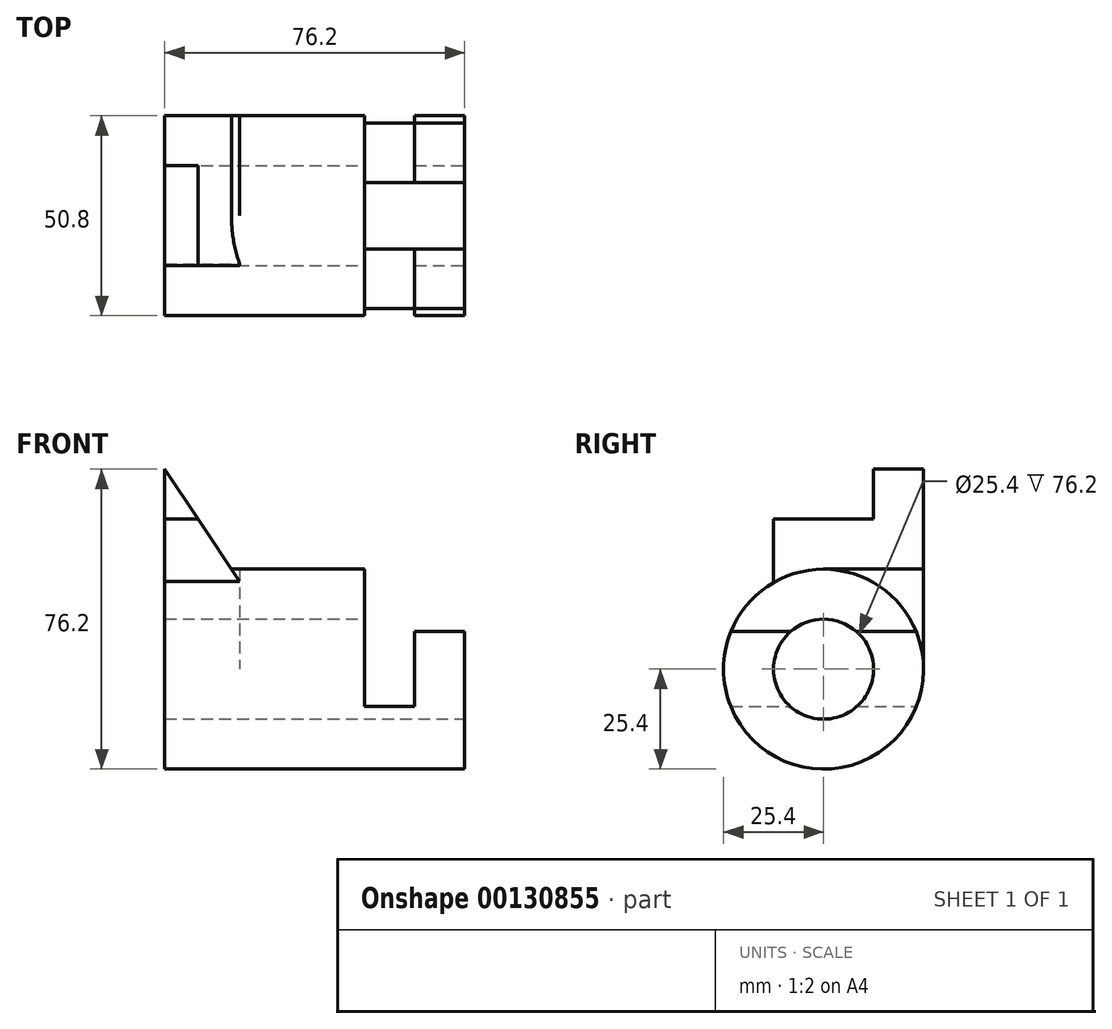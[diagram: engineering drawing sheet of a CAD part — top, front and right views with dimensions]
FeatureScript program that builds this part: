
annotation { "Feature Type Name" : "Feature", "Feature Type Description" : "" }
export const myFeature = defineFeature(function(context is Context, id is Id, definition is map)
    precondition{}
    {
        {
            var Q0;
            Q0=qCreatedBy(makeId("Right.planeOp"),FACE);
            var sketch = newSketch(context, id + "F0", { "sketchPlane" : qUnion([Q0])});
            skCircle(sketch, "E0", {"center": v(0, 0) * mm, "radius": 12.7 * mm});
            skCircle(sketch, "E1", {"center": v(0, 0) * mm, "radius": 25.4 * mm});
            skLineSegment(sketch, "E2", {"start": v(25.4, 0) * mm, "end": v(25.4, 50.8) * mm});
            skLineSegment(sketch, "E3", {"start": v(25.4, 50.8) * mm, "end": v(12.7, 50.8) * mm});
            skLineSegment(sketch, "E4", {"start": v(12.7, 50.8) * mm, "end": v(12.7, 38.1) * mm});
            skLineSegment(sketch, "E5", {"start": v(12.7, 38.1) * mm, "end": v(-12.7, 38.1) * mm});
            skLineSegment(sketch, "E6", {"start": v(-12.7, 38.1) * mm, "end": v(-12.7, 22) * mm});
            skLineSegment(sketch, "E7", {"start": v(-8.4, 9.53) * mm, "end": v(-23.55, 9.53) * mm});
            skLineSegment(sketch, "E8", {"start": v(8.4, 9.53) * mm, "end": v(23.55, 9.53) * mm});
            skLineSegment(sketch, "E9", {"start": v(0, 0) * mm, "end": v(-25.4, 0) * mm, "construction": true});
            skLineSegment(sketch, "E10", {"start": v(-25.4, 0) * mm, "end": v(-25.4, 25.4) * mm});
            skLineSegment(sketch, "E11", {"start": v(-25.4, 25.4) * mm, "end": v(0, 25.4) * mm});
            skLineSegment(sketch, "E12.MirrorCS", {"start": v(25.4, 25.4) * mm, "end": v(0, 25.4) * mm});
            skLineSegment(sketch, "E13.MirrorCS", {"start": v(25.4, 0) * mm, "end": v(25.4, 25.4) * mm});
            skLineSegment(sketch, "E14", {"start": v(12.7, 50.8) * mm, "end": v(-25.4, 50.8) * mm});
            skLineSegment(sketch, "E15", {"start": v(-25.4, 50.8) * mm, "end": v(-25.4, 25.4) * mm});
            skLineSegment(sketch, "E16", {"start": v(-25.4, 0) * mm, "end": v(-25.4, -25.4) * mm});
            skLineSegment(sketch, "E17", {"start": v(-25.4, -25.4) * mm, "end": v(0, -25.4) * mm});
            skLineSegment(sketch, "E18.MirrorCS", {"start": v(25.4, 0) * mm, "end": v(25.4, -25.4) * mm});
            skLineSegment(sketch, "E19.MirrorCS", {"start": v(25.4, -25.4) * mm, "end": v(0, -25.4) * mm});
            skSolve(sketch);
        }
        {
            var Q0;
            Q0=qCreatedBy(makeId("Front.planeOp"),FACE);
            var sketch = newSketch(context, id + "F1", { "sketchPlane" : qUnion([Q0])});
            skLineSegment(sketch, "E20", {"start": v(0, 0) * mm, "end": v(0, 9.53) * mm});
            skLineSegment(sketch, "E21", {"start": v(0, 9.53) * mm, "end": v(-12.7, 9.53) * mm});
            skLineSegment(sketch, "E22", {"start": v(0, 0) * mm, "end": v(0, -25.4) * mm});
            skLineSegment(sketch, "E23", {"start": v(0, -25.4) * mm, "end": v(-76.2, -25.4) * mm});
            skLineSegment(sketch, "E24", {"start": v(-76.2, -25.4) * mm, "end": v(-76.2, 50.8) * mm});
            skLineSegment(sketch, "E25", {"start": v(-12.7, 9.53) * mm, "end": v(-12.7, -9.53) * mm});
            skLineSegment(sketch, "E26", {"start": v(-12.7, -9.53) * mm, "end": v(-25.4, -9.53) * mm});
            skLineSegment(sketch, "E27", {"start": v(-25.4, -9.53) * mm, "end": v(-25.4, 25.4) * mm});
            skLineSegment(sketch, "E28", {"start": v(-25.4, 25.4) * mm, "end": v(-59.27, 25.4) * mm});
            skLineSegment(sketch, "E29", {"start": v(-76.2, 50.8) * mm, "end": v(-57.15, 22.22) * mm});
            skLineSegment(sketch, "E30", {"start": v(-57.15, 22.22) * mm, "end": v(-76.2, 22.22) * mm});
            skLineSegment(sketch, "E31", {"start": v(-59.27, 25.4) * mm, "end": v(-76.2, 25.4) * mm});
            skLineSegment(sketch, "E32", {"start": v(-76.2, 25.4) * mm, "end": v(-76.2, 22.22) * mm});
            skSolve(sketch);
        }
        {
            var Q0;
            Q0 = qSketchRegion(id + "F1", true);
            extrude(context, id + "F2", {"entities" : qUnion([Q0]), "endBound" : BoundingType.SYMMETRIC, "depth" : 50.8 * mm});
        }
        {
            var Q0;
            {var subQ0=sQuery(id+"F0.wireOp",EDGE,"E0");var subQ1=makeQuery(id+"F0.imprint","INTERSECT",VERTEX,{"derivedFrom":[subQ0,sQuery(id+"F0.wireOp",EDGE,"E7")]});Q0=makeQuery(id+"F0.imprint","IMPRINT",FACE,{"disambiguationData":[TD([[makeQuery(id+"F0.imprint","IMPRINT",EDGE,{"disambiguationData":[TD([[subQ1,1.0]])],"derivedFrom":subQ0}),1.0]])]});}
            extrude(context, id + "F3", {"entities" : qUnion([Q0]), "operationType" : NewBodyOperationType.REMOVE, "oppositeDirection" : true, "depth" : 254 * mm});
        }
        {
            var Q0;
            {var subQ0=sQuery(id+"F0.wireOp",EDGE,"E6");var subQ1=sQuery(id+"F0.wireOp",EDGE,"E1");var subQ2=makeQuery(id+"F0.imprint","INTERSECT",VERTEX,{"derivedFrom":[subQ1,subQ0]});Q0=makeQuery(id+"F0.imprint","IMPRINT",FACE,{"disambiguationData":[TD([[makeQuery(id+"F0.imprint","IMPRINT",EDGE,{"disambiguationData":[TD([[subQ2,1.0]])],"derivedFrom":subQ1}),-1.0]])]});}
            var Q1;
            {var subQ0=sQuery(id+"F0.wireOp",EDGE,"E10");Q1=makeQuery(id+"F0.imprint","IMPRINT",FACE,{"disambiguationData":[TD([[makeQuery(id+"F0.imprint","IMPRINT",EDGE,{"derivedFrom":subQ0}),-1.0]])]});}
            extrude(context, id + "F4", {"entities" : qUnion([Q0, Q1]), "operationType" : NewBodyOperationType.REMOVE, "oppositeDirection" : true, "depth" : 105.4 * mm});
        }
        {
            var Q0;
            {var subQ3=sQuery(id+"F0.wireOp",EDGE,"E12.MirrorCS");Q0=makeQuery(id+"F0.imprint","IMPRINT",FACE,{"disambiguationData":[TD([[makeQuery(id+"F0.imprint","IMPRINT",EDGE,{"derivedFrom":subQ3}),1.0]])]});}
            extrude(context, id + "F5", {"entities" : qUnion([Q0]), "operationType" : NewBodyOperationType.REMOVE, "oppositeDirection" : true, "depth" : 381 * mm});
        }
        {
            var Q0;
            Q0=makeQuery(id+"F0.imprint","IMPRINT",FACE,{"disambiguationData":[TD([[makeQuery(id+"F0.imprint","IMPRINT",EDGE,{"derivedFrom":sQuery(id+"F0.wireOp",EDGE,"E4")}),-1.0]])]});
            extrude(context, id + "F6", {"entities" : qUnion([Q0]), "operationType" : NewBodyOperationType.REMOVE, "oppositeDirection" : true, "depth" : 127 * mm});
        }
        {
            var Q0;
            {var subQ0=sQuery(id+"F1.wireOp",EDGE,"E29");var subQ5=sQuery(id+"F1.wireOp",EDGE,"E24");Q0=makeQuery(id+"F5.boolean.opBoolean","SPLIT",FACE,{"disambiguationData":[TD([makeQuery(id+"F2.opExtrude","SWEPT_FACE",FACE,{"disambiguationData":[OSD([subQ0])]})])],"derivedFrom":makeQuery(id+"F2.opExtrude","SWEPT_FACE",FACE,{"disambiguationData":[OSD([subQ5])]})});}
            var sketch = newSketch(context, id + "F7", { "sketchPlane" : qUnion([Q0])});
            skLineSegment(sketch, "E33", {"start": v(-25.4, 25.4) * mm, "end": v(-25.4, 0) * mm});
            skLineSegment(sketch, "E34", {"start": v(-25.4, 25.4) * mm, "end": v(0, 25.4) * mm});
            skArc(sketch, "E35", {"start": v(-25.4, 0) * mm, "mid": v(-17.96, 17.96) * mm, "end": v(0, 25.4) * mm});
            skSolve(sketch);
        }
        {
            var Q0;
            Q0=makeQuery(id+"F7.imprint","IMPRINT",FACE,{"disambiguationData":[TD([[makeQuery(id+"F7.imprint","IMPRINT",EDGE,{"derivedFrom":sQuery(id+"F7.wireOp",EDGE,"E33")}),1.0]])]});
            extrude(context, id + "F8", {"entities" : qUnion([Q0]), "operationType" : NewBodyOperationType.ADD, "oppositeDirection" : true, "depth" : 19.05 * mm});
        }
        {
            var Q0;
            {var subQ2=sQuery(id+"F1.wireOp",EDGE,"E30");Q0=makeQuery(id+"F1.imprint","IMPRINT",FACE,{"disambiguationData":[TD([[makeQuery(id+"F1.imprint","IMPRINT",EDGE,{"derivedFrom":subQ2}),-1.0]])]});}
            extrude(context, id + "F9", {"entities" : qUnion([Q0]), "operationType" : NewBodyOperationType.ADD, "depth" : 12.7 * mm});
        }
        {
            var Q0;
            {var subQ0=sQuery(id+"F0.wireOp",EDGE,"E16");Q0=makeQuery(id+"F0.imprint","IMPRINT",FACE,{"disambiguationData":[TD([[makeQuery(id+"F0.imprint","IMPRINT",EDGE,{"derivedFrom":subQ0}),1.0]])]});}
            var Q1;
            {var subQ0=sQuery(id+"F0.wireOp",EDGE,"E18.MirrorCS");Q1=makeQuery(id+"F0.imprint","IMPRINT",FACE,{"disambiguationData":[TD([[makeQuery(id+"F0.imprint","IMPRINT",EDGE,{"derivedFrom":subQ0}),-1.0]])]});}
            extrude(context, id + "F10", {"entities" : qUnion([Q0, Q1]), "operationType" : NewBodyOperationType.REMOVE, "oppositeDirection" : true, "depth" : 254 * mm});
        }
    });
